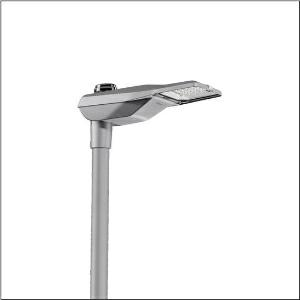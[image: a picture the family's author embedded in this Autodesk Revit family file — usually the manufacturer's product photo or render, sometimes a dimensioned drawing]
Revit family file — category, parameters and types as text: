
# Revit family: streetlight_sl_21_micro___st1_0a_5xe5d57n08db_813c
name_source: partatom
category: Lighting Fixtures
units: mm (PartAtom-declared; Revit-internal decimal feet)

## family parameters
Cut with Voids When Loaded = No
Host = Face
Light Source = No
Part Type = Normal
Room Calculation Point = No
Round Connector Dimension = Use Diameter
Shared = No

## types (1)
- --- (1 x LED, 4400 lm, 39.1 W, 3000K)
    Apparent Load = 39 VA
    CIE Flux Codes = 37 72 97 100 100
    Color Rendering = 80
    Color Temperature = 3000K
    Default Elevation = 1800 mm
    Description = Streetlight SL 21 micro, mast luminaire, primary light control with lens, of PMMA, primary optical cover: cover, of toughened safety glass, transparent, light distribution: ST1.0a, light emission: direct distribution, primary light characteristic: asymmetric, installation type: post-top, LED, 3G 1.5mm², High Power LED, rated luminous flux: 4.400lm, luminous efficacy: 113lm/W, light colour: 830, colour temperature: 3000K, control: overheat protection, presetting dimming linear, constant luminous flux control, time-dependent luminous flux control, flexible luminous flux parameterisation, mains connection: 230..240V, AC, 50/60Hz, connection cable pre-assembled, cable length: 6,5m, wiring characteristics: H07RN-F, start of lifetime: 39W, end of service life: 41W, reduction: 18W, luminaire housing, of diecast aluminium (EN AC-44300), powder-coated, Siteco® metallic grey (DB 702S), corrosivity category C5 mid according to DIN EN ISO 12944, multi-level sealing system, sealing non-destructively replaceable, inclination adjustable: 0°, 5°, 10°, 15°, length: 528mm, width: 235mm, height: 110mm, spigot size: 76/60mm (post-top), protection rating (complete): IP66, insulation class (complete): insulation class I (protective earthing), certification: CE, ENEC, ENEC+, VDE, impact resistance: IK09, permissible operating ambient temperature for outdoor applications: -40..+50°C, standard-compliant lighting for roads and squares, packaging unit: 1 piece

Light Distribution: ST1.0a
    Height = 110 mm
    Lamp = 1 x LED
    Lamp Light Flux = 4400 lm
    Lamp Power = 39.1 W
    Lamp count = 1
    Length = 528 mm
    Luminous efficacy = 113 lm/W
    Manufacturer = Siteco
    ModVariant = No
    Model = 5XE5D57N08DB
    Number of Poles = 1
    OnlyDefault = Yes
    Power Factor = 1
    Product Name = Streetlight SL 21 micro | ST1.0a
    Product group = mast luminaire | pylon top
    ProductGroupID = 6100
    Protection Class = Protection class I
    Protection Degree = IP 66
    RLX_Detail_Level = 1
    RLX_Emergency_Light_Flux = 0 lm
    RLX_Emergency_Type = 0
    RLX_Emergency_Type_DB = No
    RlxData = <blob elided: 99033 chars, md5=29c2c102>
    Socket = socket
    Standby Power = 0 W
    System Light Flux = 4400 lm
    System Power = 39 W
    Type Comments = factory setting: luminous flux: 100 % | dim-lin: 254 | 765 mA
    Type Image = l_1294375.jpg
    URL = http://relux.com
    VarID = @adj_085815
    Voltage = 0 V
    Weight = 0.00 kg
    Width = 235 mm

## geometry (parser evidence)
native form markers: Blend x4, Sweep x9
no freeform markers — native parametric forms only
